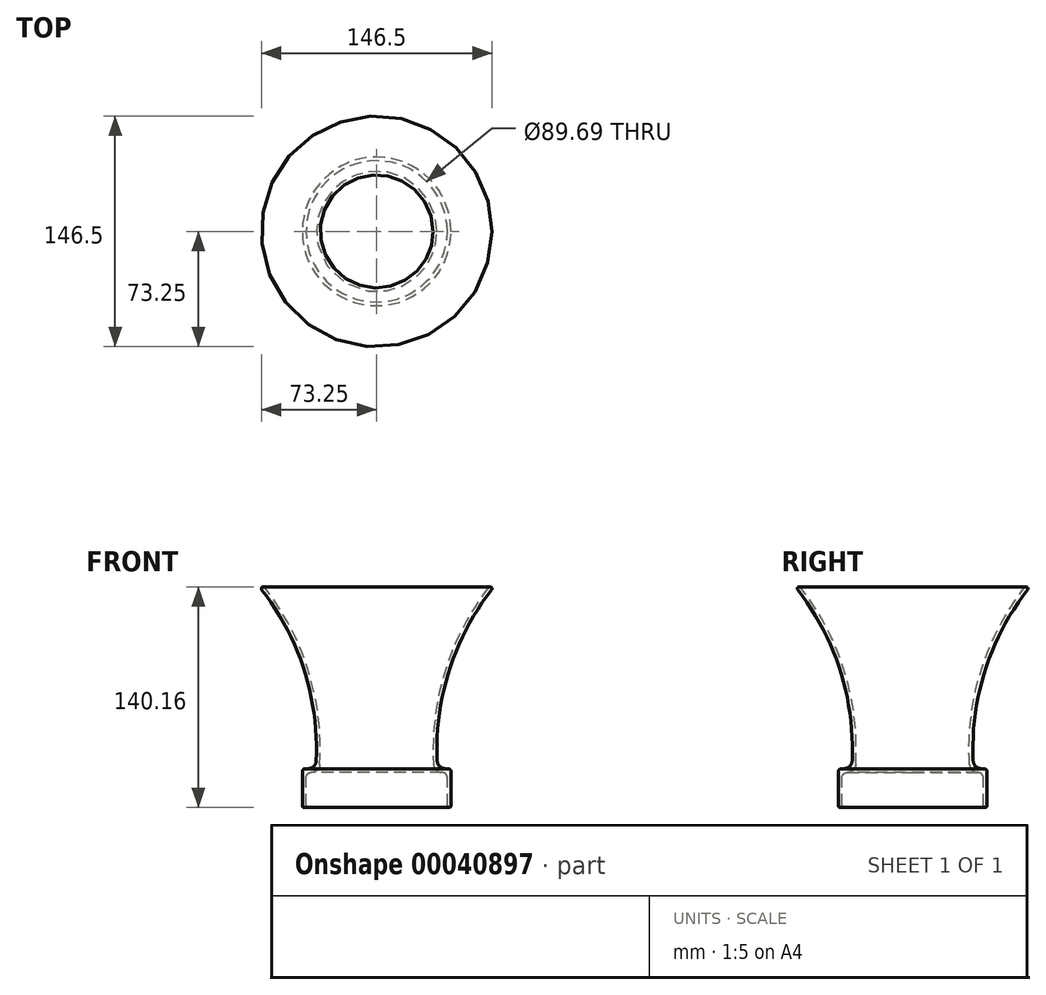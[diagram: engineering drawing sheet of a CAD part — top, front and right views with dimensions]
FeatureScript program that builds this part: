
annotation { "Feature Type Name" : "Feature", "Feature Type Description" : "" }
export const myFeature = defineFeature(function(context is Context, id is Id, definition is map)
    precondition{}
    {
        {
            var Q0;
            Q0=qCreatedBy(makeId("Front.planeOp"),FACE);
            var sketch = newSketch(context, id + "F0", { "sketchPlane" : qUnion([Q0])});
            skLineSegment(sketch, "E0", {"start": v(44.85, 1.2) * mm, "end": v(44.85, 18.92) * mm});
            skLineSegment(sketch, "E1", {"start": v(41.47, 22.23) * mm, "end": v(41.54, 22.23) * mm});
            skLineSegment(sketch, "E2", {"start": v(36.51, 22.22) * mm, "end": v(71.12, 139.7) * mm, "construction": true});
            skArc(sketch, "E3", {"start": v(71.12, 139.7) * mm, "mid": v(43.41, 86.65) * mm, "end": v(36.14, 27.25) * mm});
            skLineSegment(sketch, "E4", {"start": v(0, 74.34) * mm, "end": v(0, 0) * mm});
            skLineSegment(sketch, "E5.0", {"start": v(47.23, 1.2) * mm, "end": v(47.23, 22.7) * mm});
            skLineSegment(sketch, "E5.1", {"start": v(43.73, 24.6) * mm, "end": v(45.32, 24.6) * mm});
            skArc(sketch, "E5.2", {"start": v(73, 138.24) * mm, "mid": v(46.04, 87.05) * mm, "end": v(38.4, 29.7) * mm});
            skPoint(sketch, "E6.visualSharp", {"position": v(38.7, 24.6) * mm});
            skArc(sketch, "E6.filletArc", {"start": v(38.4, 29.7) * mm, "mid": v(40.04, 26.09) * mm, "end": v(43.73, 24.6) * mm});
            skPoint(sketch, "E7.visualSharp", {"position": v(44.85, 22.23) * mm});
            skArc(sketch, "E7.filletArc", {"start": v(44.85, 18.92) * mm, "mid": v(43.88, 21.26) * mm, "end": v(41.54, 22.23) * mm});
            skPoint(sketch, "E8.visualSharp", {"position": v(36.51, 22.23) * mm});
            skArc(sketch, "E8.filletArc", {"start": v(36.14, 27.25) * mm, "mid": v(37.8, 23.68) * mm, "end": v(41.47, 22.23) * mm});
            skArc(sketch, "E9", {"start": v(44.85, 1.2) * mm, "mid": v(46.04, 0) * mm, "end": v(47.23, 1.2) * mm});
            skArc(sketch, "E10", {"start": v(71.12, 139.7) * mm, "mid": v(72.8, 139.9) * mm, "end": v(73, 138.24) * mm});
            skPoint(sketch, "E11.visualSharp", {"position": v(47.23, 24.6) * mm});
            skArc(sketch, "E11.filletArc", {"start": v(47.23, 22.7) * mm, "mid": v(46.67, 24.05) * mm, "end": v(45.32, 24.6) * mm});
            skPoint(sketch, "E12", {"position": v(46.04, 0) * mm});
            skSolve(sketch);
        }
        {
            var Q0;
            Q0 = qSketchRegion(id + "F0", true);
            var Q1;
            Q1=sQuery(id+"F0.wireOp",EDGE,"E4");
            revolve(context, id + "F1", {"entities" : qUnion([Q0]), "axis" : qUnion([Q1]), "revolveType" : RevolveType.FULL});
        }
    });
